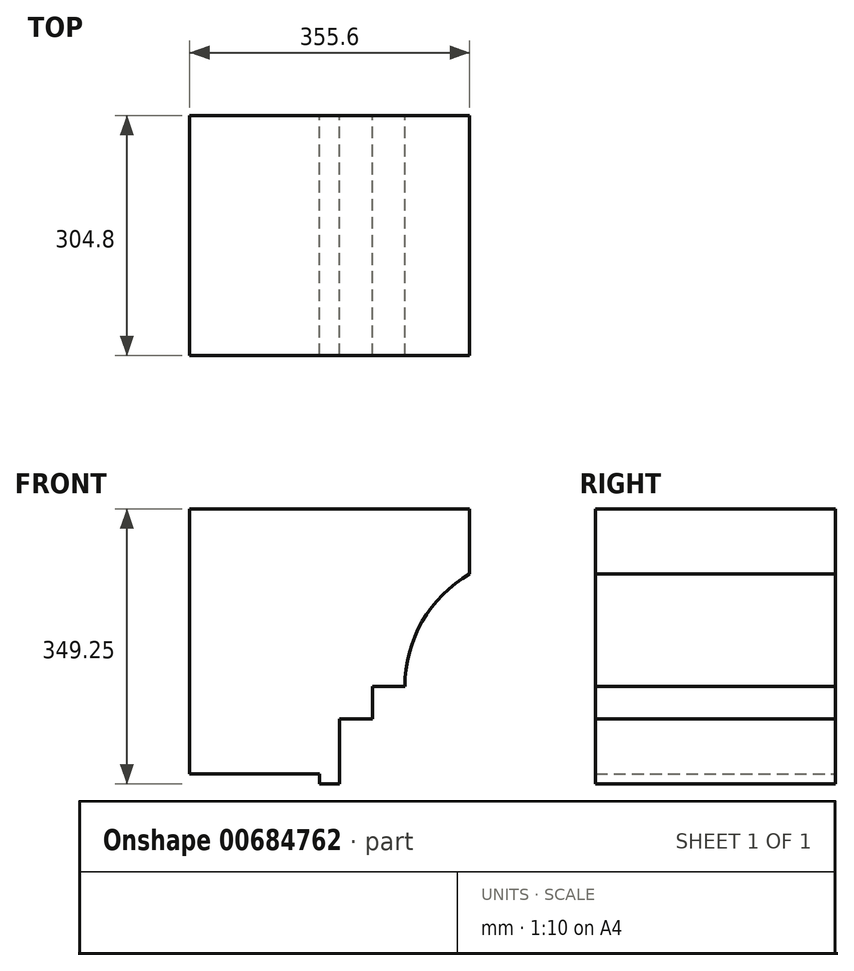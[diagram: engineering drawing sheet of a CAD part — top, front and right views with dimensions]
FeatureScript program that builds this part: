
annotation { "Feature Type Name" : "Feature", "Feature Type Description" : "" }
export const myFeature = defineFeature(function(context is Context, id is Id, definition is map)
    precondition{}
    {
        {
            var Q0;
            Q0=qCreatedBy(makeId("Front.planeOp"),FACE);
            var sketch = newSketch(context, id + "F0", { "sketchPlane" : qUnion([Q0])});
            skLineSegment(sketch, "E0", {"start": v(273.14, -225.38) * mm, "end": v(231.82, -225.38) * mm});
            skLineSegment(sketch, "E1", {"start": v(231.82, -225.38) * mm, "end": v(231.82, -266.7) * mm});
            skLineSegment(sketch, "E2", {"start": v(231.82, -266.7) * mm, "end": v(190.5, -266.7) * mm});
            skLineSegment(sketch, "E3", {"start": v(190.5, -266.7) * mm, "end": v(190.5, -349.25) * mm});
            skLineSegment(sketch, "E4", {"start": v(0, 0) * mm, "end": v(355.6, 0) * mm});
            skLineSegment(sketch, "E5", {"start": v(355.6, 0) * mm, "end": v(355.6, -82.55) * mm});
            skArc(sketch, "E6", {"start": v(355.6, -82.55) * mm, "mid": v(295.23, -142.92) * mm, "end": v(273.14, -225.38) * mm});
            skLineSegment(sketch, "E7", {"start": v(273.14, -225.38) * mm, "end": v(438.06, -225.38) * mm, "construction": true});
            skPoint(sketch, "E8", {"position": v(355.6, -225.38) * mm});
            skLineSegment(sketch, "E9", {"start": v(0, -336.55) * mm, "end": v(0, -336.55) * mm});
            skLineSegment(sketch, "E10", {"start": v(0, -336.55) * mm, "end": v(0, 0) * mm});
            skLineSegment(sketch, "E11", {"start": v(190.5, -349.25) * mm, "end": v(165.1, -349.25) * mm});
            skLineSegment(sketch, "E12", {"start": v(165.1, -349.25) * mm, "end": v(165.1, -336.55) * mm});
            skLineSegment(sketch, "E13", {"start": v(165.1, -336.55) * mm, "end": v(0, -336.55) * mm});
            skSolve(sketch);
        }
        {
            var Q0;
            Q0=qSketchRegion(id+"F0",true);
            extrude(context, id + "F1", {"entities" : qUnion([Q0]), "endBound" : BoundingType.SYMMETRIC, "depth" : 304.8 * mm, "offsetDistance" : 25.4 * mm});
        }
    });
